# Revit family: Cassettes slim
name_source: partatom
category: Installations électriques
units: mm (PartAtom-declared; Revit-internal decimal feet)

## family parameters
Basée sur le plan de construction = Non
Conserver l'orientation des annotations = Non
Cote de connecteur circulaire = Utiliser le diamètre
Couper avec des vides une fois chargée = Non
Partagée = Non
Point de calcul de pièce = Non
Toujours verticalement = Oui
Type d'élément = Normal

## types (3) — shared parameters
Classe ETIM = EC002699
Couleur = IDS_NOIR
Croisé = Oui
Fonction = Cassettes haute densité MTP
Hauteur = 13.6 mm  [stored 0.0446194 ft]
Largeur (mm) = 100 mm  [stored 0.328084 ft]
Lien e-catalogue = https://www.legrand.fr
Nombre de connecteurs face arrière = 1
Nombre de connecteurs face avant = 12
Profondeur = 194 mm  [stored 0.636483 ft]
Température de fonctionnement = -10°C à 60°C
Température de stockage = -10°C à 60°C
Type de connecteur externe = LC_DUPLEX
Type de connecteur interne = MTP-M
zero-valued in all types: Elévation par défaut

## per-type parameters (varying)
| type | Classe de fibre optique | Connecteurs LC | EAN | Référence Legrand |
| Cassette compacte 12 LC MTP OM3 panneau HD Ultra | OM3 | Connecteurs LC slim : 12 fibres OM3 multimode | 3414971929333 | 032168 |
| Cassette compacte 12 LC MTP OM4 panneau HD Ultra | OM4 | Connecteurs LC slim : 12 fibres OM4 multimode | 3414971929135 | 032169 |
| Cassette compacte 12 LC MTP OS2 panneau HD Ultra | OS2 | Connecteurs LC slim : 12 fibres OS2 monomode | 3414971929159 | 032170 |

note: column(s) folded — value = type name in every type: Libellé BIM

note: [stored X ft] marks values corroborated as IEEE doubles in the binary element streams (Revit-internal decimal feet)
